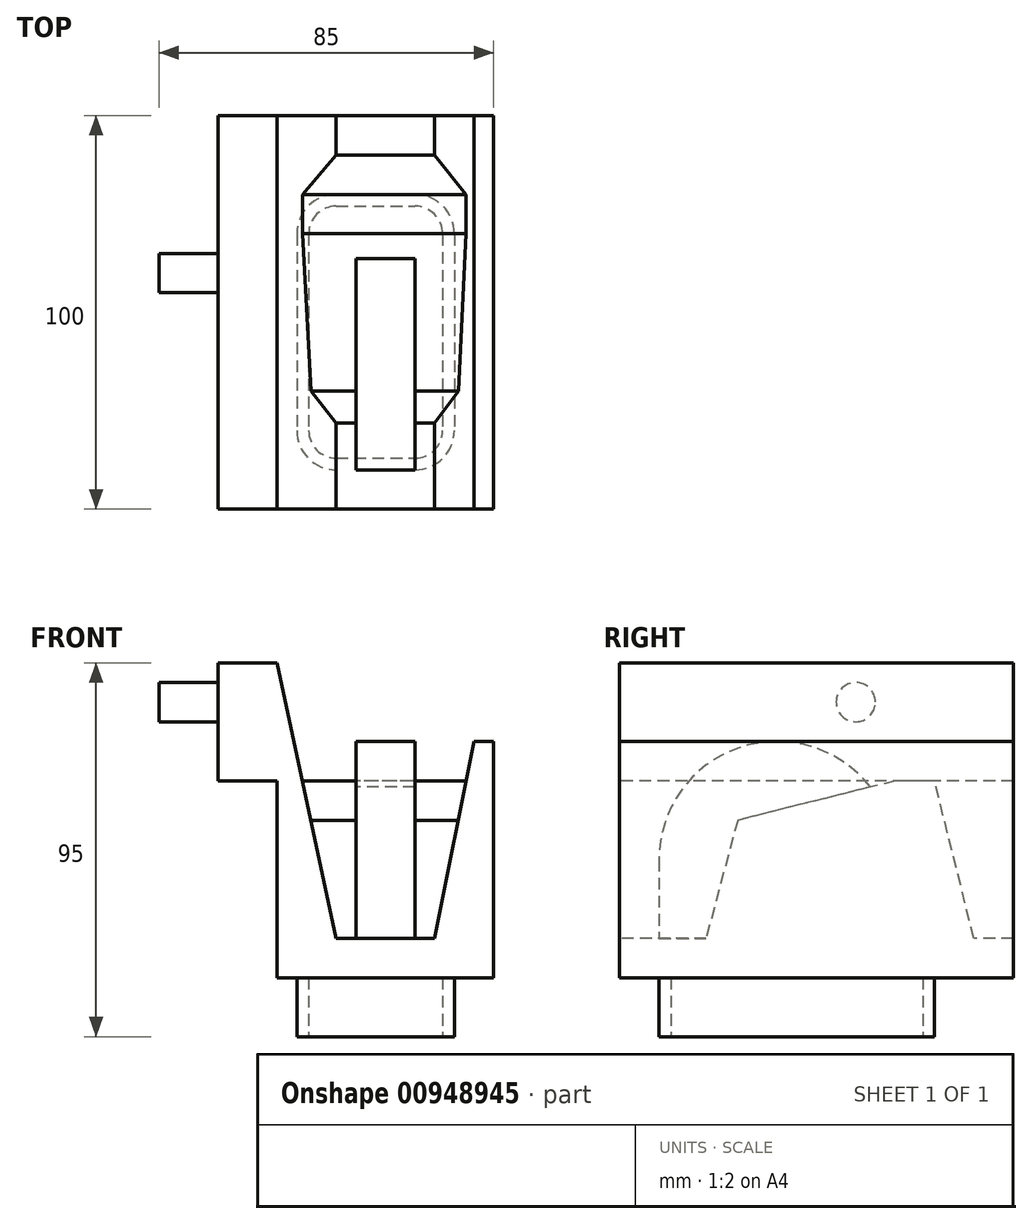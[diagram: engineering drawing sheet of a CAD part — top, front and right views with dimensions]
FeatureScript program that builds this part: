
annotation { "Feature Type Name" : "Feature", "Feature Type Description" : "" }
export const myFeature = defineFeature(function(context is Context, id is Id, definition is map)
    precondition{}
    {
        {
            var Q0;
            Q0=qCreatedBy(makeId("Front.planeOp"),FACE);
            var sketch = newSketch(context, id + "F0", { "sketchPlane" : qUnion([Q0])});
            skLineSegment(sketch, "E0", {"start": v(0, 80) * mm, "end": v(0, 0) * mm});
            skLineSegment(sketch, "E1", {"start": v(0, 0) * mm, "end": v(55, 0) * mm});
            skLineSegment(sketch, "E2", {"start": v(55, 0) * mm, "end": v(55, 60) * mm});
            skLineSegment(sketch, "E3", {"start": v(55, 60) * mm, "end": v(50, 60) * mm});
            skLineSegment(sketch, "E4", {"start": v(50, 60) * mm, "end": v(40, 10) * mm});
            skLineSegment(sketch, "E5", {"start": v(40, 10) * mm, "end": v(15, 10) * mm});
            skLineSegment(sketch, "E6", {"start": v(15, 10) * mm, "end": v(0, 80) * mm});
            skSolve(sketch);
        }
        {
            var Q0;
            Q0 = qSketchRegion(id + "F0", true);
            extrude(context, id + "F1", {"entities" : qUnion([Q0]), "oppositeDirection" : true, "depth" : 100 * mm, "offsetDistance" : 25 * mm});
        }
        {
            var Q0;
            Q0=makeQuery(id+"F1.opExtrude","SWEPT_FACE",FACE,{"disambiguationData":[OSD([sQuery(id+"F0.wireOp",EDGE,"E2")])]});
            cPlane(context, id + "F2", {"entities" : qUnion([Q0]), "cplaneType" : CPlaneType.OFFSET, "offset" : 27.5 * mm, "oppositeDirection" : true, "width" : 150 * mm, "height" : 150 * mm});
        }
        {
            var Q0;
            Q0=qCreatedBy(id+"F2.planeOp",FACE);
            var sketch = newSketch(context, id + "F3", { "sketchPlane" : qUnion([Q0])});
            skLineSegment(sketch, "E7", {"start": v(21.96, 10) * mm, "end": v(90, 10) * mm});
            skLineSegment(sketch, "E8", {"start": v(90, 10) * mm, "end": v(80, 50) * mm});
            skLineSegment(sketch, "E9", {"start": v(80, 50) * mm, "end": v(70, 50) * mm});
            skLineSegment(sketch, "E10", {"start": v(70, 50) * mm, "end": v(30, 40) * mm});
            skLineSegment(sketch, "E11", {"start": v(30, 40) * mm, "end": v(21.96, 10) * mm});
            skLineSegment(sketch, "E12", {"start": v(30, 40) * mm, "end": v(30, 10) * mm, "construction": true});
            skSolve(sketch);
        }
        {
            var Q0;
            Q0 = qSketchRegion(id + "F3", true);
            extrude(context, id + "F4", {"entities" : qUnion([Q0]), "operationType" : NewBodyOperationType.ADD, "endBound" : BoundingType.UP_TO_NEXT, "depth" : 25 * mm, "offsetDistance" : 25 * mm, "hasSecondDirection" : true, "secondDirectionBound" : SecondDirectionBoundingType.UP_TO_NEXT, "secondDirectionOppositeDirection" : true, "secondDirectionDepth" : 25 * mm});
        }
        {
            var Q0;
            Q0=qCreatedBy(id+"F2.planeOp",FACE);
            var sketch = newSketch(context, id + "F5", { "sketchPlane" : qUnion([Q0])});
            skArc(sketch, "E13", {"start": v(40, 0) * mm, "mid": v(61.21, 51.21) * mm, "end": v(10, 30) * mm});
            skLineSegment(sketch, "E14", {"start": v(10, 30) * mm, "end": v(10, 0) * mm});
            skLineSegment(sketch, "E15", {"start": v(10, 0) * mm, "end": v(40, 0) * mm});
            skSolve(sketch);
        }
        {
            var Q0;
            Q0 = qSketchRegion(id + "F5", true);
            extrude(context, id + "F6", {"entities" : qUnion([Q0]), "operationType" : NewBodyOperationType.ADD, "depth" : 7.5 * mm, "offsetDistance" : 25 * mm, "hasSecondDirection" : true, "secondDirectionOppositeDirection" : true, "secondDirectionDepth" : 7.5 * mm});
        }
        {
            var Q0;
            Q0=makeQuery(id+"F1.opExtrude","CAP_FACE",FACE,{"disambiguationData":[OSD([sQuery(id+"F0.wireOp",EDGE,"E0"),sQuery(id+"F0.wireOp",EDGE,"E1"),sQuery(id+"F0.wireOp",EDGE,"E2"),sQuery(id+"F0.wireOp",EDGE,"E3"),sQuery(id+"F0.wireOp",EDGE,"E4"),sQuery(id+"F0.wireOp",EDGE,"E5"),sQuery(id+"F0.wireOp",EDGE,"E6")])],"isStart":true});
            var sketch = newSketch(context, id + "F7", { "sketchPlane" : qUnion([Q0])});
            skLineSegment(sketch, "E16.bottom", {"start": v(0, 80) * mm, "end": v(-15, 80) * mm});
            skLineSegment(sketch, "E16.top", {"start": v(0, 50) * mm, "end": v(-15, 50) * mm});
            skLineSegment(sketch, "E16.left", {"start": v(0, 80) * mm, "end": v(0, 50) * mm});
            skLineSegment(sketch, "E16.right", {"start": v(-15, 80) * mm, "end": v(-15, 50) * mm});
            skSolve(sketch);
        }
        {
            var Q0;
            Q0 = qSketchRegion(id + "F7", true);
            extrude(context, id + "F8", {"entities" : qUnion([Q0]), "operationType" : NewBodyOperationType.ADD, "oppositeDirection" : true, "depth" : 100 * mm, "offsetDistance" : 25 * mm});
        }
        {
            var Q0;
            Q0=makeQuery(id+"F8.opExtrude","SWEPT_FACE",FACE,{"disambiguationData":[OSD([sQuery(id+"F7.wireOp",EDGE,"E16.right")])]});
            var sketch = newSketch(context, id + "F9", { "sketchPlane" : qUnion([Q0])});
            skCircle(sketch, "E17", {"center": v(-60, 70) * mm, "radius": 5 * mm});
            skSolve(sketch);
        }
        {
            var Q0;
            Q0 = qSketchRegion(id + "F9", true);
            extrude(context, id + "F10", {"entities" : qUnion([Q0]), "operationType" : NewBodyOperationType.ADD, "depth" : 15 * mm, "offsetDistance" : 25 * mm});
        }
        {
            var Q0;
            Q0=makeQuery(id+"F1.opExtrude","SWEPT_FACE",FACE,{"disambiguationData":[OSD([sQuery(id+"F0.wireOp",EDGE,"E1")])]});
            var sketch = newSketch(context, id + "F11", { "sketchPlane" : qUnion([Q0])});
            skLineSegment(sketch, "E18.bottom", {"start": v(5, -80) * mm, "end": v(45, -80) * mm});
            skLineSegment(sketch, "E18.top", {"start": v(5, -10) * mm, "end": v(45, -10) * mm});
            skLineSegment(sketch, "E18.left", {"start": v(5, -80) * mm, "end": v(5, -10) * mm});
            skLineSegment(sketch, "E18.right", {"start": v(45, -80) * mm, "end": v(45, -10) * mm});
            skSolve(sketch);
        }
        {
            var Q0;
            Q0 = qSketchRegion(id + "F11", true);
            extrude(context, id + "F12", {"entities" : qUnion([Q0]), "operationType" : NewBodyOperationType.ADD, "depth" : 15 * mm, "offsetDistance" : 25 * mm});
        }
        {
            var Q0;
            Q0=makeQuery(id+"F12.opExtrude","SWEPT_EDGE",EDGE,{"disambiguationData":[OSD([sQuery(id+"F11.wireOp",EDGE,"E18.top"),sQuery(id+"F11.wireOp",EDGE,"E18.right")])]});
            var Q1;
            Q1=makeQuery(id+"F12.opExtrude","SWEPT_EDGE",EDGE,{"disambiguationData":[OSD([sQuery(id+"F11.wireOp",EDGE,"E18.top"),sQuery(id+"F11.wireOp",EDGE,"E18.left")])]});
            var Q2;
            Q2=makeQuery(id+"F12.opExtrude","SWEPT_EDGE",EDGE,{"disambiguationData":[OSD([sQuery(id+"F11.wireOp",EDGE,"E18.bottom"),sQuery(id+"F11.wireOp",EDGE,"E18.right")])]});
            var Q3;
            Q3=makeQuery(id+"F12.opExtrude","SWEPT_EDGE",EDGE,{"disambiguationData":[OSD([sQuery(id+"F11.wireOp",EDGE,"E18.bottom"),sQuery(id+"F11.wireOp",EDGE,"E18.left")])]});
            fillet(context, id + "F13", {"entities" : qUnion([Q0, Q1, Q2, Q3]), "radius" : 10 * mm, "tangentPropagation" : true, "allowEdgeOverflow" : false});
        }
        {
            var Q0;
            Q0=makeQuery(id+"F12.opExtrude","CAP_FACE",FACE,{"disambiguationData":[OSD([sQuery(id+"F11.wireOp",EDGE,"E18.bottom"),sQuery(id+"F11.wireOp",EDGE,"E18.top"),sQuery(id+"F11.wireOp",EDGE,"E18.left"),sQuery(id+"F11.wireOp",EDGE,"E18.right")])],"isStart":false});
            var sketch = newSketch(context, id + "F14", { "sketchPlane" : qUnion([Q0])});
            skArc(sketch, "E19.0", {"start": v(8, -70) * mm, "mid": v(10.05, -74.95) * mm, "end": v(15, -77) * mm});
            skLineSegment(sketch, "E19.1", {"start": v(15, -77) * mm, "end": v(35, -77) * mm});
            skLineSegment(sketch, "E19.2", {"start": v(8, -70) * mm, "end": v(8, -20) * mm});
            skArc(sketch, "E19.3", {"start": v(35, -77) * mm, "mid": v(39.95, -74.95) * mm, "end": v(42, -70) * mm});
            skArc(sketch, "E19.4", {"start": v(15, -13) * mm, "mid": v(10.05, -15.05) * mm, "end": v(8, -20) * mm});
            skLineSegment(sketch, "E19.5", {"start": v(15, -13) * mm, "end": v(35, -13) * mm});
            skArc(sketch, "E19.6", {"start": v(42, -20) * mm, "mid": v(39.95, -15.05) * mm, "end": v(35, -13) * mm});
            skLineSegment(sketch, "E19.7", {"start": v(42, -70) * mm, "end": v(42, -20) * mm});
            skSolve(sketch);
        }
        {
            var Q0;
            Q0 = qSketchRegion(id + "F14", true);
            extrude(context, id + "F15", {"entities" : qUnion([Q0]), "operationType" : NewBodyOperationType.REMOVE, "oppositeDirection" : true, "depth" : 15 * mm, "offsetDistance" : 25 * mm});
        }
    });
